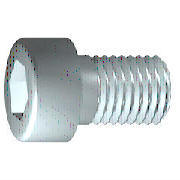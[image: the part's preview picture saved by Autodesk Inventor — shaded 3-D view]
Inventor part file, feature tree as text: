
AUTODESK INVENTOR PART (.ipt)
format: ipt  version: 2021 (Build 250183000, 183)  size: 196,096 bytes
history: native  units: mm (DEFAULTED — no unit token found)
features: sketch x2, extrude x1, plane x1, fillet x1
ambient origin geometry x7: Origin, YZ Plane, XY Plane, X Axis, Y Axis, Z Axis, Center Point
bodies: Solid1 (feature_tree), Body (feature_tree)
feature tree (5):
  extrude  "Slot"  Depth=3.0mm
  plane  "Work Plane1"
  fillet  "Fillet2"  Radius=3.0mm
  sketch  "Sketch1"  dims[d1=6.75mm d2=0.306825mm d3=3.0mm]
  sketch  "Sketch2"  dims[d4=1.3mm d5=60.0deg d6=3.0mm d7=3.0mm d8=2.886751mm d9=5.5mm d10=90.0deg d11=10.0mm d12=0.0mm d13=6.75mm d14=0.0mm d15=0.306725mm d16=0.306725mm d17=0.3mm d19=0.0mm d26=8.0mm d27=45.0deg d28=0.0mm d29=0.0mm d30=0.1mm]
